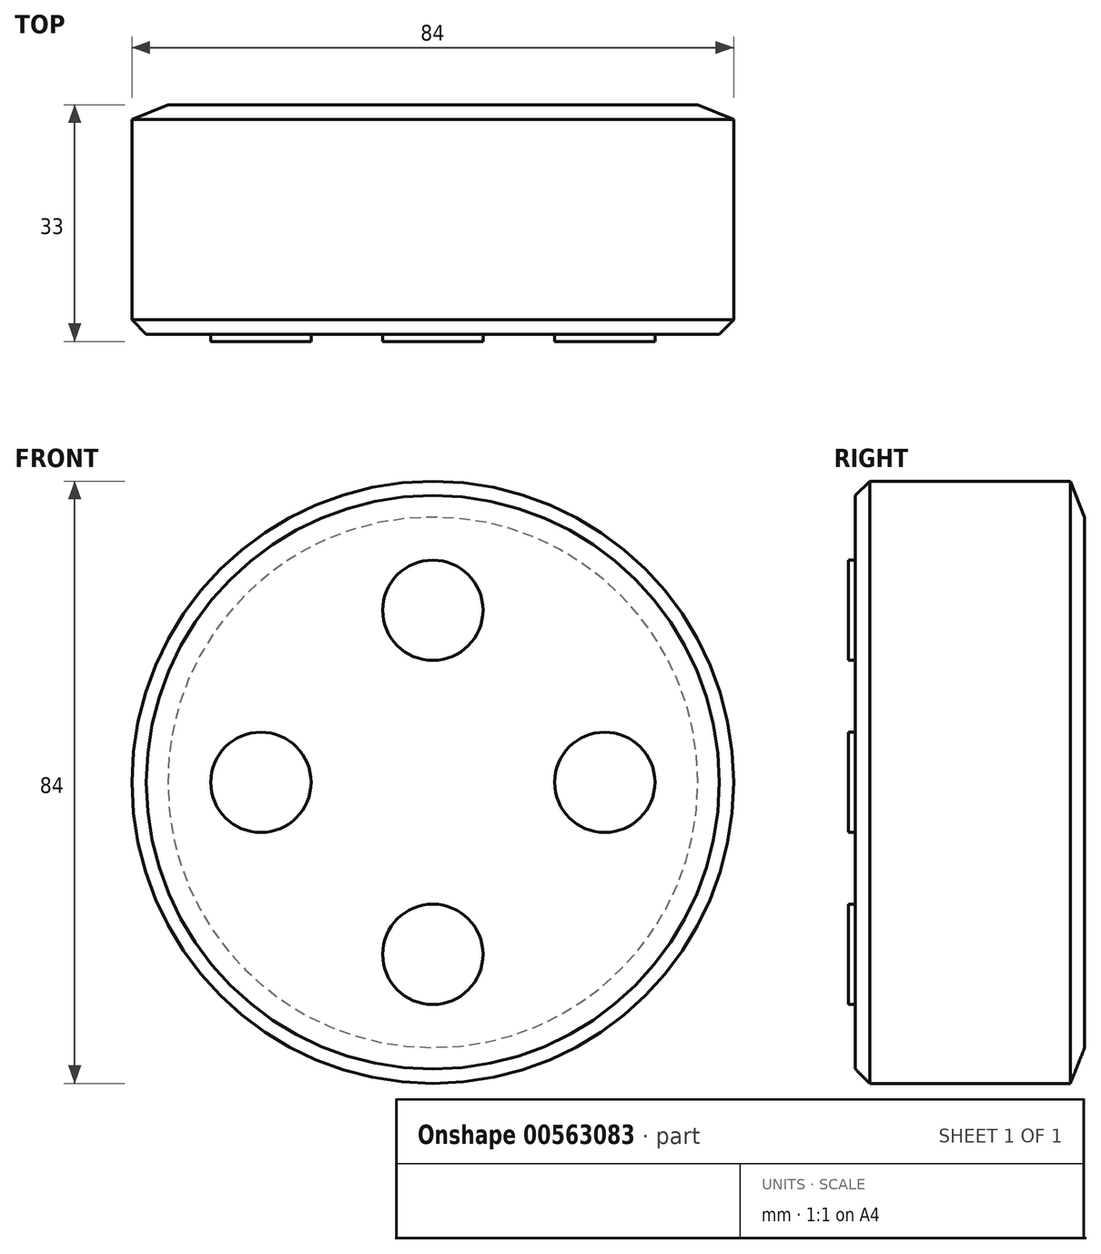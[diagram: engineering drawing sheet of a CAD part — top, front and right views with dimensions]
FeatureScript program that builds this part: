
annotation { "Feature Type Name" : "Feature", "Feature Type Description" : "" }
export const myFeature = defineFeature(function(context is Context, id is Id, definition is map)
    precondition{}
    {
        {
            var Q0;
            Q0=qCreatedBy(makeId("Front.planeOp"),FACE);
            var sketch = newSketch(context, id + "F0", { "sketchPlane" : qUnion([Q0])});
            skCircle(sketch, "E0", {"center": v(0, 0) * mm, "radius": 42 * mm});
            skSolve(sketch);
        }
        {
            var Q0;
            Q0=qSketchRegion(id+"F0",true);
            extrude(context, id + "F1", {"entities" : qUnion([Q0]), "depth" : 32 * mm, "offsetDistance" : 25 * mm});
        }
        {
            var Q0;
            Q0=makeQuery(id+"F1.opExtrude","CAP_FACE",FACE,{"disambiguationData":[OSD([sQuery(id+"F0.wireOp",EDGE,"E0")])],"isStart":true});
            chamfer(context, id + "F2", {"entities" : qUnion([Q0]), "chamferType" : ChamferType.TWO_OFFSETS, "width1" : 2 * mm, "oppositeDirection" : false, "width2" : 5 * mm, "tangentPropagation" : true});
        }
        {
            var Q0;
            Q0=makeQuery(id+"F1.opExtrude","CAP_FACE",FACE,{"disambiguationData":[OSD([sQuery(id+"F0.wireOp",EDGE,"E0")])],"isStart":false});
            chamfer(context, id + "F3", {"entities" : qUnion([Q0]), "width" : 2 * mm, "tangentPropagation" : true});
        }
        {
            var Q0;
            Q0=makeQuery(id+"F1.opExtrude","CAP_FACE",FACE,{"disambiguationData":[OSD([sQuery(id+"F0.wireOp",EDGE,"E0")])],"isStart":false});
            var sketch = newSketch(context, id + "F4", { "sketchPlane" : qUnion([Q0])});
            skLineSegment(sketch, "E1", {"start": v(-69.27, 0) * mm, "end": v(62.97, 0) * mm, "construction": true});
            skLineSegment(sketch, "E2", {"start": v(0, 50.92) * mm, "end": v(0, -47.46) * mm, "construction": true});
            skCircle(sketch, "E3", {"center": v(-24, 0) * mm, "radius": 7 * mm});
            skCircle(sketch, "E4.MirrorC", {"center": v(24, 0) * mm, "radius": 7 * mm});
            skCircle(sketch, "E5", {"center": v(0, 0) * mm, "radius": 24 * mm, "construction": true});
            skCircle(sketch, "E6", {"center": v(0, 24) * mm, "radius": 7 * mm});
            skCircle(sketch, "E7.MirrorC", {"center": v(0, -24) * mm, "radius": 7 * mm});
            skSolve(sketch);
        }
        {
            var Q0;
            Q0=qSketchRegion(id+"F4",true);
            extrude(context, id + "F5", {"entities" : qUnion([Q0]), "operationType" : NewBodyOperationType.ADD, "depth" : 1 * mm, "offsetDistance" : 25 * mm});
        }
    });
